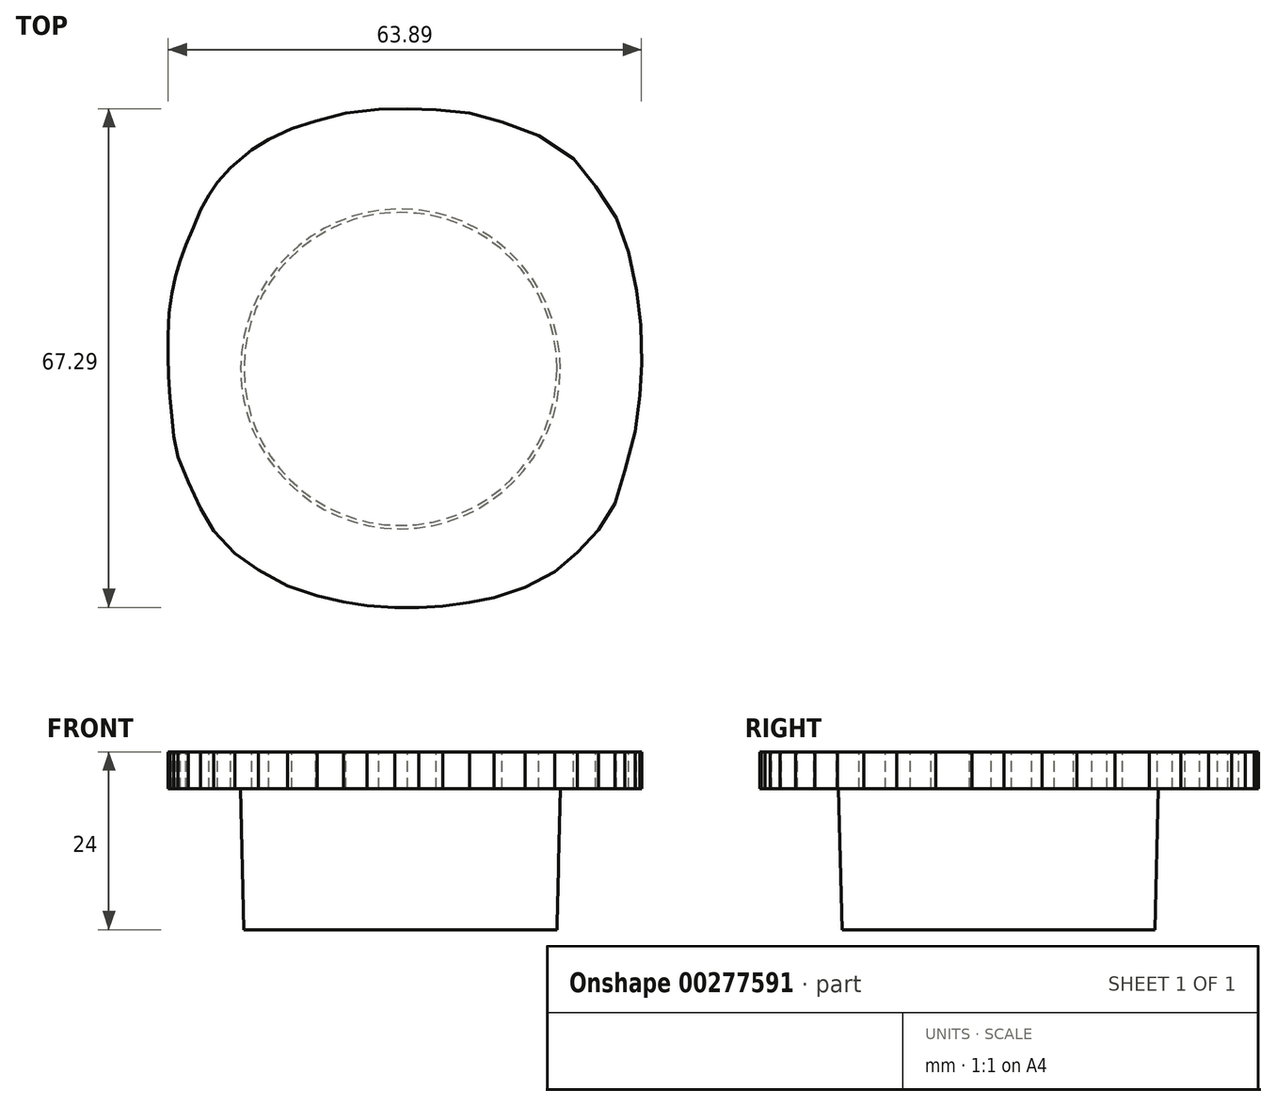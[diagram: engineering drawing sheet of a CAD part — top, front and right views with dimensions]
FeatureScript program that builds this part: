
annotation { "Feature Type Name" : "Feature", "Feature Type Description" : "" }
export const myFeature = defineFeature(function(context is Context, id is Id, definition is map)
    precondition{}
    {
        {
            var Q0;
            Q0=qCreatedBy(makeId("Top.planeOp"),FACE);
            var sketch = newSketch(context, id + "F0", { "sketchPlane" : qUnion([Q0])});
            skCircle(sketch, "E0", {"center": v(0, 0) * mm, "radius": 21.12 * mm});
            skSolve(sketch);
        }
        {
            var Q0;
            Q0=qCreatedBy(makeId("Top.planeOp"),FACE);
            cPlane(context, id + "F1", {"entities" : qUnion([Q0]), "cplaneType" : CPlaneType.OFFSET, "offset" : 19 * mm, "width" : 150 * mm, "height" : 150 * mm});
        }
        {
            var Q0;
            Q0=qCreatedBy(id+"F1.planeOp",FACE);
            var sketch = newSketch(context, id + "F2", { "sketchPlane" : qUnion([Q0])});
            skCircle(sketch, "E1", {"center": v(0, 0) * mm, "radius": 21.58 * mm});
            skSolve(sketch);
        }
        {
            var Q0;
            Q0=makeQuery(id+"F2.imprint","IMPRINT",FACE,{"disambiguationData":[TD([[makeQuery(id+"F2.imprint","IMPRINT",EDGE,{"derivedFrom":sQuery(id+"F2.wireOp",EDGE,"E1")}),1.0]])]});
            cPlane(context, id + "F3", {"entities" : qUnion([Q0]), "cplaneType" : CPlaneType.OFFSET, "offset" : 5 * mm, "width" : 150 * mm, "height" : 150 * mm});
        }
        {
            var Q0;
            Q0=qCreatedBy(id+"F3.planeOp",FACE);
            var sketch = newSketch(context, id + "F4", { "sketchPlane" : qUnion([Q0])});
            skLineSegment(sketch, "E2", {"start": v(0.95, 35.11) * mm, "end": v(-2.95, 35.04) * mm});
            skLineSegment(sketch, "E3", {"start": v(-2.95, 35.04) * mm, "end": v(-7.39, 34.5) * mm});
            skLineSegment(sketch, "E4", {"start": v(-7.39, 34.5) * mm, "end": v(-11.44, 33.43) * mm});
            skLineSegment(sketch, "E5", {"start": v(-11.44, 33.43) * mm, "end": v(-14.65, 32.44) * mm});
            skLineSegment(sketch, "E6", {"start": v(-14.65, 32.44) * mm, "end": v(-17.79, 30.98) * mm});
            skLineSegment(sketch, "E7", {"start": v(-17.79, 30.98) * mm, "end": v(-20.08, 29.6) * mm});
            skLineSegment(sketch, "E8", {"start": v(-20.08, 29.6) * mm, "end": v(-22.91, 27.16) * mm});
            skLineSegment(sketch, "E9", {"start": v(-22.91, 27.16) * mm, "end": v(-24.67, 25.17) * mm});
            skLineSegment(sketch, "E10", {"start": v(-24.67, 25.17) * mm, "end": v(-25.82, 23.49) * mm});
            skLineSegment(sketch, "E11", {"start": v(-25.82, 23.49) * mm, "end": v(-26.97, 21.42) * mm});
            skLineSegment(sketch, "E12", {"start": v(-26.97, 21.42) * mm, "end": v(-27.96, 19.13) * mm});
            skLineSegment(sketch, "E13", {"start": v(-27.96, 19.13) * mm, "end": v(-28.98, 16.73) * mm});
            skLineSegment(sketch, "E14", {"start": v(-28.98, 16.73) * mm, "end": v(-29.73, 14.67) * mm});
            skLineSegment(sketch, "E15", {"start": v(-29.73, 14.67) * mm, "end": v(-30.36, 12.6) * mm});
            skLineSegment(sketch, "E16", {"start": v(-30.36, 12.6) * mm, "end": v(-30.86, 10.13) * mm});
            skLineSegment(sketch, "E17", {"start": v(-30.86, 10.13) * mm, "end": v(-31.25, 7.57) * mm});
            skLineSegment(sketch, "E18", {"start": v(-31.25, 7.57) * mm, "end": v(-31.35, 4.5) * mm});
            skLineSegment(sketch, "E19", {"start": v(-31.35, 4.5) * mm, "end": v(-31.35, 1.75) * mm});
            skLineSegment(sketch, "E20", {"start": v(-31.35, 1.75) * mm, "end": v(-31.3, -0.95) * mm});
            skLineSegment(sketch, "E21", {"start": v(-31.3, -0.95) * mm, "end": v(-31.14, -3.92) * mm});
            skLineSegment(sketch, "E22", {"start": v(-31.14, -3.92) * mm, "end": v(-30.89, -6.37) * mm});
            skLineSegment(sketch, "E23", {"start": v(-30.89, -6.37) * mm, "end": v(-30.58, -9.07) * mm});
            skLineSegment(sketch, "E24", {"start": v(-30.58, -9.07) * mm, "end": v(-30.02, -11.88) * mm});
            skLineSegment(sketch, "E25", {"start": v(-30.02, -11.88) * mm, "end": v(-28.65, -15.24) * mm});
            skLineSegment(sketch, "E26", {"start": v(-28.65, -15.24) * mm, "end": v(-27.01, -18.82) * mm});
            skLineSegment(sketch, "E27", {"start": v(-27.01, -18.82) * mm, "end": v(-25.19, -21.86) * mm});
            skLineSegment(sketch, "E28", {"start": v(-25.19, -21.86) * mm, "end": v(-22.34, -24.9) * mm});
            skLineSegment(sketch, "E29", {"start": v(-22.34, -24.9) * mm, "end": v(-19.18, -27.14) * mm});
            skLineSegment(sketch, "E30", {"start": v(-19.18, -27.14) * mm, "end": v(-15.23, -29.27) * mm});
            skLineSegment(sketch, "E31", {"start": v(-15.23, -29.27) * mm, "end": v(-11.23, -30.6) * mm});
            skLineSegment(sketch, "E32", {"start": v(-11.23, -30.6) * mm, "end": v(-7.7, -31.45) * mm});
            skLineSegment(sketch, "E33", {"start": v(-7.7, -31.45) * mm, "end": v(-4.49, -31.94) * mm});
            skLineSegment(sketch, "E34", {"start": v(-4.49, -31.94) * mm, "end": v(-0.79, -32.18) * mm});
            skLineSegment(sketch, "E35", {"start": v(-0.79, -32.18) * mm, "end": v(2.5, -32.18) * mm});
            skLineSegment(sketch, "E36", {"start": v(2.5, -32.18) * mm, "end": v(5.71, -32) * mm});
            skLineSegment(sketch, "E37", {"start": v(5.71, -32) * mm, "end": v(9.35, -31.51) * mm});
            skLineSegment(sketch, "E38", {"start": v(9.35, -31.51) * mm, "end": v(12.63, -30.84) * mm});
            skLineSegment(sketch, "E39", {"start": v(12.63, -30.84) * mm, "end": v(16.82, -29.45) * mm});
            skLineSegment(sketch, "E40", {"start": v(16.82, -29.45) * mm, "end": v(20.83, -27.38) * mm});
            skLineSegment(sketch, "E41", {"start": v(20.83, -27.38) * mm, "end": v(23.86, -24.77) * mm});
            skLineSegment(sketch, "E42", {"start": v(23.86, -24.77) * mm, "end": v(26.72, -21.74) * mm});
            skLineSegment(sketch, "E43", {"start": v(26.72, -21.74) * mm, "end": v(28.96, -18.16) * mm});
            skLineSegment(sketch, "E44", {"start": v(28.96, -18.16) * mm, "end": v(30.3, -13.72) * mm});
            skLineSegment(sketch, "E45", {"start": v(30.3, -13.72) * mm, "end": v(31.7, -8.44) * mm});
            skLineSegment(sketch, "E46", {"start": v(31.7, -8.44) * mm, "end": v(32.3, -3.59) * mm});
            skLineSegment(sketch, "E47", {"start": v(32.3, -3.59) * mm, "end": v(32.54, 0.72) * mm});
            skLineSegment(sketch, "E48", {"start": v(32.54, 0.72) * mm, "end": v(32.43, 5.91) * mm});
            skLineSegment(sketch, "E49", {"start": v(32.43, 5.91) * mm, "end": v(31.86, 10.6) * mm});
            skLineSegment(sketch, "E50", {"start": v(31.86, 10.6) * mm, "end": v(30.77, 15.73) * mm});
            skLineSegment(sketch, "E51", {"start": v(30.77, 15.73) * mm, "end": v(29.11, 20.35) * mm});
            skLineSegment(sketch, "E52", {"start": v(29.11, 20.35) * mm, "end": v(26.37, 24.6) * mm});
            skLineSegment(sketch, "E53", {"start": v(26.37, 24.6) * mm, "end": v(23.34, 28.36) * mm});
            skLineSegment(sketch, "E54", {"start": v(23.34, 28.36) * mm, "end": v(18.64, 31.47) * mm});
            skLineSegment(sketch, "E55", {"start": v(18.64, 31.47) * mm, "end": v(13.73, 33.35) * mm});
            skLineSegment(sketch, "E56", {"start": v(13.73, 33.35) * mm, "end": v(9.33, 34.5) * mm});
            skLineSegment(sketch, "E57", {"start": v(9.33, 34.5) * mm, "end": v(4.85, 35) * mm});
            skLineSegment(sketch, "E58", {"start": v(4.85, 35) * mm, "end": v(0.95, 35.11) * mm});
            skCircle(sketch, "E59", {"center": v(-0.08, 0) * mm, "radius": 28.17 * mm, "construction": true});
            skSolve(sketch);
        }
        {
            var Q0;
            Q0=makeQuery(id+"F0.imprint","IMPRINT",FACE,{"disambiguationData":[TD([[makeQuery(id+"F0.imprint","IMPRINT",EDGE,{"derivedFrom":sQuery(id+"F0.wireOp",EDGE,"E0")}),1.0]])]});
            var Q1;
            Q1=makeQuery(id+"F2.imprint","IMPRINT",FACE,{"disambiguationData":[TD([[makeQuery(id+"F2.imprint","IMPRINT",EDGE,{"derivedFrom":sQuery(id+"F2.wireOp",EDGE,"E1")}),1.0]])]});
            loft(context, id + "F5", {"sheetProfilesArray" : [{ "sheetProfileEntities" : qUnion([Q0]) }, { "sheetProfileEntities" : qUnion([Q1]) }]});
        }
        {
            var Q0;
            Q0 = qSketchRegion(id + "F4", true);
            var Q1;
            Q1=makeQuery(id+"F5.opLoft","CAP_FACE",FACE,{"disambiguationData":[OSD([makeQuery(id+"F2.imprint","IMPRINT",FACE,{"disambiguationData":[TD([[makeQuery(id+"F2.imprint","IMPRINT",EDGE,{"derivedFrom":sQuery(id+"F2.wireOp",EDGE,"E1")}),1.0]])]})])],"isStart":true});
            extrude(context, id + "F6", {"entities" : qUnion([Q0]), "operationType" : NewBodyOperationType.ADD, "endBound" : BoundingType.UP_TO_SURFACE, "oppositeDirection" : true, "endBoundEntityFace" : qUnion([Q1]), "depth" : 25 * mm});
        }
        {
            var Q0;
            Q0=makeQuery(id+"F6.opExtrude","CAP_FACE",FACE,{"disambiguationData":[OSD([sQuery(id+"F4.wireOp",EDGE,"E2"),sQuery(id+"F4.wireOp",EDGE,"E3"),sQuery(id+"F4.wireOp",EDGE,"E4"),sQuery(id+"F4.wireOp",EDGE,"E5"),sQuery(id+"F4.wireOp",EDGE,"E6"),sQuery(id+"F4.wireOp",EDGE,"E7"),sQuery(id+"F4.wireOp",EDGE,"E8"),sQuery(id+"F4.wireOp",EDGE,"E9"),sQuery(id+"F4.wireOp",EDGE,"E10"),sQuery(id+"F4.wireOp",EDGE,"E11"),sQuery(id+"F4.wireOp",EDGE,"E12"),sQuery(id+"F4.wireOp",EDGE,"E13"),sQuery(id+"F4.wireOp",EDGE,"E14"),sQuery(id+"F4.wireOp",EDGE,"E15"),sQuery(id+"F4.wireOp",EDGE,"E16"),sQuery(id+"F4.wireOp",EDGE,"E17"),sQuery(id+"F4.wireOp",EDGE,"E18"),sQuery(id+"F4.wireOp",EDGE,"E19"),sQuery(id+"F4.wireOp",EDGE,"E20"),sQuery(id+"F4.wireOp",EDGE,"E21"),sQuery(id+"F4.wireOp",EDGE,"E22"),sQuery(id+"F4.wireOp",EDGE,"E23"),sQuery(id+"F4.wireOp",EDGE,"E24"),sQuery(id+"F4.wireOp",EDGE,"E25"),sQuery(id+"F4.wireOp",EDGE,"E26"),sQuery(id+"F4.wireOp",EDGE,"E27"),sQuery(id+"F4.wireOp",EDGE,"E28"),sQuery(id+"F4.wireOp",EDGE,"E29"),sQuery(id+"F4.wireOp",EDGE,"E30"),sQuery(id+"F4.wireOp",EDGE,"E31"),sQuery(id+"F4.wireOp",EDGE,"E32"),sQuery(id+"F4.wireOp",EDGE,"E33"),sQuery(id+"F4.wireOp",EDGE,"E34"),sQuery(id+"F4.wireOp",EDGE,"E35"),sQuery(id+"F4.wireOp",EDGE,"E36"),sQuery(id+"F4.wireOp",EDGE,"E37"),sQuery(id+"F4.wireOp",EDGE,"E38"),sQuery(id+"F4.wireOp",EDGE,"E39"),sQuery(id+"F4.wireOp",EDGE,"E40"),sQuery(id+"F4.wireOp",EDGE,"E41"),sQuery(id+"F4.wireOp",EDGE,"E42"),sQuery(id+"F4.wireOp",EDGE,"E43"),sQuery(id+"F4.wireOp",EDGE,"E44"),sQuery(id+"F4.wireOp",EDGE,"E45"),sQuery(id+"F4.wireOp",EDGE,"E46"),sQuery(id+"F4.wireOp",EDGE,"E47"),sQuery(id+"F4.wireOp",EDGE,"E48"),sQuery(id+"F4.wireOp",EDGE,"E49"),sQuery(id+"F4.wireOp",EDGE,"E50"),sQuery(id+"F4.wireOp",EDGE,"E51"),sQuery(id+"F4.wireOp",EDGE,"E52"),sQuery(id+"F4.wireOp",EDGE,"E53"),sQuery(id+"F4.wireOp",EDGE,"E54"),sQuery(id+"F4.wireOp",EDGE,"E55"),sQuery(id+"F4.wireOp",EDGE,"E56"),sQuery(id+"F4.wireOp",EDGE,"E57"),sQuery(id+"F4.wireOp",EDGE,"E58")])],"isStart":true});
            cPlane(context, id + "F7", {"entities" : qUnion([Q0]), "cplaneType" : CPlaneType.OFFSET, "offset" : 27 * mm, "width" : 150 * mm, "height" : 150 * mm});
        }
    });
